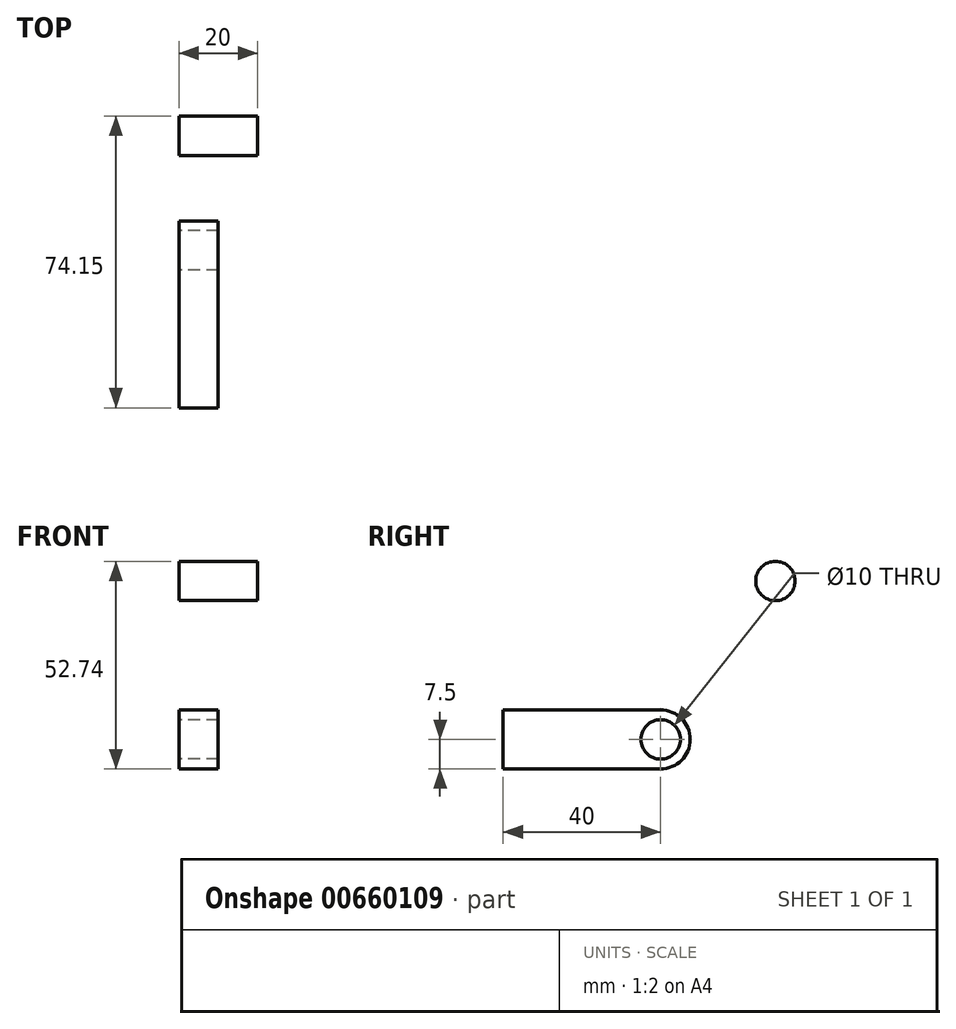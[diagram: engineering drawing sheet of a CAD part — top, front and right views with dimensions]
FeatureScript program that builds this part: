
annotation { "Feature Type Name" : "Feature", "Feature Type Description" : "" }
export const myFeature = defineFeature(function(context is Context, id is Id, definition is map)
    precondition{}
    {
        {
            var Q0;
            Q0=qCreatedBy(makeId("Right.planeOp"),FACE);
            var sketch = newSketch(context, id + "F0", { "sketchPlane" : qUnion([Q0])});
            skCircle(sketch, "E0", {"center": v(0, 0) * mm, "radius": 7.5 * mm});
            skLineSegment(sketch, "E1", {"start": v(0, 7.5) * mm, "end": v(-40, 7.5) * mm});
            skLineSegment(sketch, "E2", {"start": v(0, -7.5) * mm, "end": v(-40, -7.5) * mm});
            skLineSegment(sketch, "E3", {"start": v(-40, -7.5) * mm, "end": v(-40, 7.5) * mm});
            skCircle(sketch, "E4", {"center": v(0, 0) * mm, "radius": 5 * mm});
            skSolve(sketch);
        }
        {
            var Q0;
            Q0 = qSketchRegion(id + "F0", true);
            extrude(context, id + "F1", {"entities" : qUnion([Q0]), "depth" : 10 * mm, "offsetDistance" : 25 * mm});
        }
        {
            var Q0;
            Q0=qCreatedBy(makeId("Right.planeOp"),FACE);
            var sketch = newSketch(context, id + "F2", { "sketchPlane" : qUnion([Q0])});
            skCircle(sketch, "E5", {"center": v(29.15, 40.24) * mm, "radius": 5 * mm});
            skSolve(sketch);
        }
        {
            var Q0;
            Q0 = qSketchRegion(id + "F2", true);
            extrude(context, id + "F3", {"entities" : qUnion([Q0]), "depth" : 20 * mm, "offsetDistance" : 25 * mm});
        }
    });
